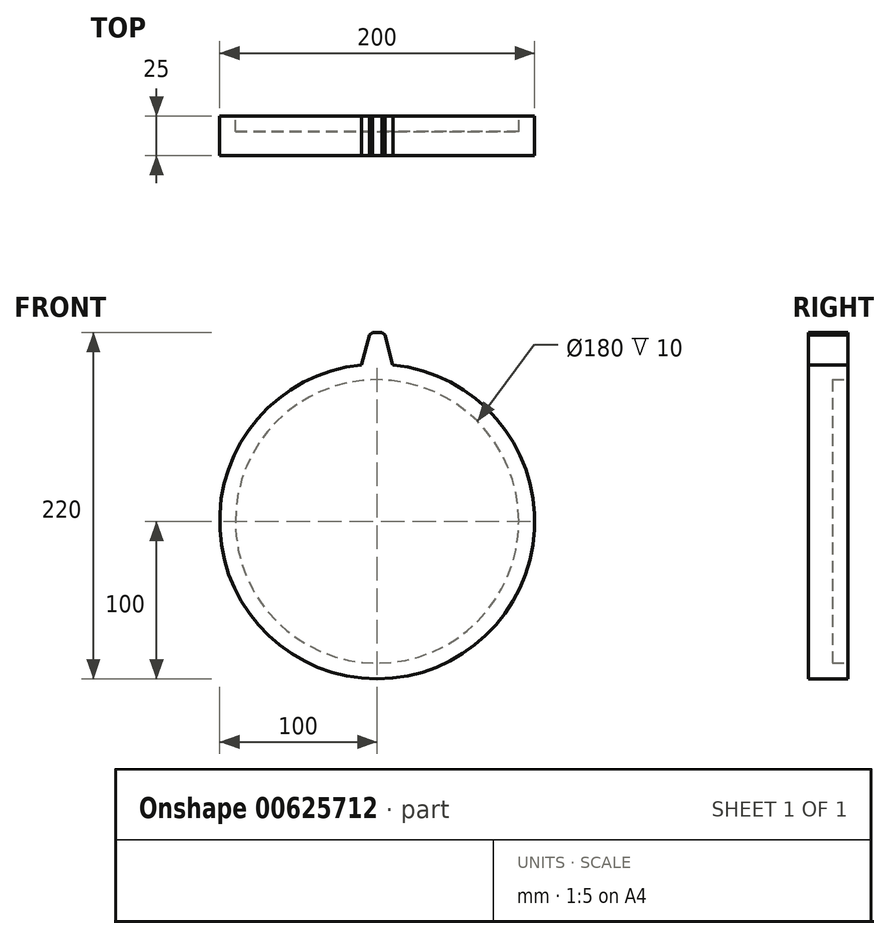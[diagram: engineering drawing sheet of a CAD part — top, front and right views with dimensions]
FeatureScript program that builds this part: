
annotation { "Feature Type Name" : "Feature", "Feature Type Description" : "" }
export const myFeature = defineFeature(function(context is Context, id is Id, definition is map)
    precondition{}
    {
        {
            var Q0;
            Q0=qCreatedBy(makeId("Front.planeOp"),FACE);
            var sketch = newSketch(context, id + "F0", { "sketchPlane" : qUnion([Q0])});
            skCircle(sketch, "E0", {"center": v(0, 0) * mm, "radius": 100 * mm});
            skSolve(sketch);
        }
        {
            var Q0;
            Q0=makeQuery(id+"F0.imprint","IMPRINT",FACE,{"disambiguationData":[TD([[makeQuery(id+"F0.imprint","IMPRINT",EDGE,{"derivedFrom":sQuery(id+"F0.wireOp",EDGE,"E0")}),1.0]])]});
            extrude(context, id + "F1", {"entities" : qUnion([Q0]), "depth" : 25 * mm, "offsetDistance" : 25 * mm});
        }
        {
            var Q0;
            Q0=qCreatedBy(makeId("Front.planeOp"),FACE);
            var sketch = newSketch(context, id + "F2", { "sketchPlane" : qUnion([Q0])});
            skLineSegment(sketch, "E1", {"start": v(-10, 99.5) * mm, "end": v(-4.5, 120) * mm});
            skLineSegment(sketch, "E2", {"start": v(-4.5, 120) * mm, "end": v(4.5, 120) * mm});
            skLineSegment(sketch, "E3", {"start": v(4.5, 120) * mm, "end": v(10, 99.5) * mm});
            skLineSegment(sketch, "E4", {"start": v(10, 99.5) * mm, "end": v(-10, 99.5) * mm});
            skSolve(sketch);
        }
        {
            var Q0;
            Q0 = qSketchRegion(id + "F2", true);
            extrude(context, id + "F3", {"entities" : qUnion([Q0]), "operationType" : NewBodyOperationType.ADD, "depth" : 25 * mm, "offsetDistance" : 25 * mm});
        }
        {
            var Q0;
            Q0=makeQuery(id+"F3.opExtrude","SWEPT_EDGE",EDGE,{"disambiguationData":[OSD([sQuery(id+"F2.wireOp",EDGE,"E1"),sQuery(id+"F2.wireOp",EDGE,"E2")])]});
            var Q1;
            Q1=makeQuery(id+"F3.opExtrude","SWEPT_EDGE",EDGE,{"disambiguationData":[OSD([sQuery(id+"F2.wireOp",EDGE,"E2"),sQuery(id+"F2.wireOp",EDGE,"E3")])]});
            chamfer(context, id + "F4", {"entities" : qUnion([Q0, Q1]), "width" : 2 * mm, "tangentPropagation" : true});
        }
        {
            var Q0;
            Q0=makeQuery(id+"F3.opExtrude","SWEPT_EDGE",EDGE,{"disambiguationData":[OSD([sQuery(id+"F2.wireOp",EDGE,"E1"),sQuery(id+"F2.wireOp",EDGE,"E4")])]});
            var Q1;
            Q1=makeQuery(id+"F3.opExtrude","SWEPT_EDGE",EDGE,{"disambiguationData":[OSD([sQuery(id+"F2.wireOp",EDGE,"E3"),sQuery(id+"F2.wireOp",EDGE,"E4")])]});
            fillet(context, id + "F5", {"entities" : qUnion([Q0, Q1]), "radius" : 5 * mm, "tangentPropagation" : true, "allowEdgeOverflow" : false});
        }
        {
            var Q0;
            {var subQ0=sQuery(id+"F2.wireOp",EDGE,"E4");var subQ1=sQuery(id+"F2.wireOp",EDGE,"E3");var subQ2=sQuery(id+"F2.wireOp",EDGE,"E2");var subQ3=sQuery(id+"F2.wireOp",EDGE,"E1");Q0=makeQuery(id+"FxM7K1GwsqZvOpN_1.19.F3.boolean.opBoolean","MERGE",FACE,{"derivedFrom":[makeQuery(id+"FxM7K1GwsqZvOpN_1.18.F3.boolean.opBoolean","MERGE",FACE,{"derivedFrom":[makeQuery(id+"FxM7K1GwsqZvOpN_1.17.F3.boolean.opBoolean","MERGE",FACE,{"derivedFrom":[makeQuery(id+"FxM7K1GwsqZvOpN_1.16.F3.boolean.opBoolean","MERGE",FACE,{"derivedFrom":[makeQuery(id+"FxM7K1GwsqZvOpN_1.15.F3.boolean.opBoolean","MERGE",FACE,{"derivedFrom":[makeQuery(id+"FxM7K1GwsqZvOpN_1.14.F3.boolean.opBoolean","MERGE",FACE,{"derivedFrom":[makeQuery(id+"FxM7K1GwsqZvOpN_1.13.F3.boolean.opBoolean","MERGE",FACE,{"derivedFrom":[makeQuery(id+"FxM7K1GwsqZvOpN_1.12.F3.boolean.opBoolean","MERGE",FACE,{"derivedFrom":[makeQuery(id+"FxM7K1GwsqZvOpN_1.11.F3.boolean.opBoolean","MERGE",FACE,{"derivedFrom":[makeQuery(id+"FxM7K1GwsqZvOpN_1.10.F3.boolean.opBoolean","MERGE",FACE,{"derivedFrom":[makeQuery(id+"FxM7K1GwsqZvOpN_1.9.F3.boolean.opBoolean","MERGE",FACE,{"derivedFrom":[makeQuery(id+"FxM7K1GwsqZvOpN_1.8.F3.boolean.opBoolean","MERGE",FACE,{"derivedFrom":[makeQuery(id+"FxM7K1GwsqZvOpN_1.7.F3.boolean.opBoolean","MERGE",FACE,{"derivedFrom":[makeQuery(id+"FxM7K1GwsqZvOpN_1.6.F3.boolean.opBoolean","MERGE",FACE,{"derivedFrom":[makeQuery(id+"FxM7K1GwsqZvOpN_1.5.F3.boolean.opBoolean","MERGE",FACE,{"derivedFrom":[makeQuery(id+"FxM7K1GwsqZvOpN_1.4.F3.boolean.opBoolean","MERGE",FACE,{"derivedFrom":[makeQuery(id+"FxM7K1GwsqZvOpN_1.3.F3.boolean.opBoolean","MERGE",FACE,{"derivedFrom":[makeQuery(id+"FxM7K1GwsqZvOpN_1.2.F3.boolean.opBoolean","MERGE",FACE,{"derivedFrom":[makeQuery(id+"FxM7K1GwsqZvOpN_1.1.F3.boolean.opBoolean","MERGE",FACE,{"derivedFrom":[makeQuery(id+"F3.boolean.opBoolean","MERGE",FACE,{"derivedFrom":[makeQuery(id+"F1.opExtrude","CAP_FACE",FACE,{"disambiguationData":[OSD([sQuery(id+"F0.wireOp",EDGE,"E0")])],"isStart":true}),makeQuery(id+"F3.opExtrude","CAP_FACE",FACE,{"disambiguationData":[OSD([subQ3,subQ2,subQ1,subQ0])],"isStart":true})]}),makeQuery(id+"FxM7K1GwsqZvOpN_1.1.F3.opExtrude","CAP_FACE",FACE,{"disambiguationData":[OSD([subQ3,subQ2,subQ1,subQ0])],"isStart":true})]}),makeQuery(id+"FxM7K1GwsqZvOpN_1.2.F3.opExtrude","CAP_FACE",FACE,{"disambiguationData":[OSD([subQ3,subQ2,subQ1,subQ0])],"isStart":true})]}),makeQuery(id+"FxM7K1GwsqZvOpN_1.3.F3.opExtrude","CAP_FACE",FACE,{"disambiguationData":[OSD([subQ3,subQ2,subQ1,subQ0])],"isStart":true})]}),makeQuery(id+"FxM7K1GwsqZvOpN_1.4.F3.opExtrude","CAP_FACE",FACE,{"disambiguationData":[OSD([subQ3,subQ2,subQ1,subQ0])],"isStart":true})]}),makeQuery(id+"FxM7K1GwsqZvOpN_1.5.F3.opExtrude","CAP_FACE",FACE,{"disambiguationData":[OSD([subQ3,subQ2,subQ1,subQ0])],"isStart":true})]}),makeQuery(id+"FxM7K1GwsqZvOpN_1.6.F3.opExtrude","CAP_FACE",FACE,{"disambiguationData":[OSD([subQ3,subQ2,subQ1,subQ0])],"isStart":true})]}),makeQuery(id+"FxM7K1GwsqZvOpN_1.7.F3.opExtrude","CAP_FACE",FACE,{"disambiguationData":[OSD([subQ3,subQ2,subQ1,subQ0])],"isStart":true})]}),makeQuery(id+"FxM7K1GwsqZvOpN_1.8.F3.opExtrude","CAP_FACE",FACE,{"disambiguationData":[OSD([subQ3,subQ2,subQ1,subQ0])],"isStart":true})]}),makeQuery(id+"FxM7K1GwsqZvOpN_1.9.F3.opExtrude","CAP_FACE",FACE,{"disambiguationData":[OSD([subQ3,subQ2,subQ1,subQ0])],"isStart":true})]}),makeQuery(id+"FxM7K1GwsqZvOpN_1.10.F3.opExtrude","CAP_FACE",FACE,{"disambiguationData":[OSD([subQ3,subQ2,subQ1,subQ0])],"isStart":true})]}),makeQuery(id+"FxM7K1GwsqZvOpN_1.11.F3.opExtrude","CAP_FACE",FACE,{"disambiguationData":[OSD([subQ3,subQ2,subQ1,subQ0])],"isStart":true})]}),makeQuery(id+"FxM7K1GwsqZvOpN_1.12.F3.opExtrude","CAP_FACE",FACE,{"disambiguationData":[OSD([subQ3,subQ2,subQ1,subQ0])],"isStart":true})]}),makeQuery(id+"FxM7K1GwsqZvOpN_1.13.F3.opExtrude","CAP_FACE",FACE,{"disambiguationData":[OSD([subQ3,subQ2,subQ1,subQ0])],"isStart":true})]}),makeQuery(id+"FxM7K1GwsqZvOpN_1.14.F3.opExtrude","CAP_FACE",FACE,{"disambiguationData":[OSD([subQ3,subQ2,subQ1,subQ0])],"isStart":true})]}),makeQuery(id+"FxM7K1GwsqZvOpN_1.15.F3.opExtrude","CAP_FACE",FACE,{"disambiguationData":[OSD([subQ3,subQ2,subQ1,subQ0])],"isStart":true})]}),makeQuery(id+"FxM7K1GwsqZvOpN_1.16.F3.opExtrude","CAP_FACE",FACE,{"disambiguationData":[OSD([subQ3,subQ2,subQ1,subQ0])],"isStart":true})]}),makeQuery(id+"FxM7K1GwsqZvOpN_1.17.F3.opExtrude","CAP_FACE",FACE,{"disambiguationData":[OSD([subQ3,subQ2,subQ1,subQ0])],"isStart":true})]}),makeQuery(id+"FxM7K1GwsqZvOpN_1.18.F3.opExtrude","CAP_FACE",FACE,{"disambiguationData":[OSD([subQ3,subQ2,subQ1,subQ0])],"isStart":true})]}),makeQuery(id+"FxM7K1GwsqZvOpN_1.19.F3.opExtrude","CAP_FACE",FACE,{"disambiguationData":[OSD([subQ3,subQ2,subQ1,subQ0])],"isStart":true})]});}
            var sketch = newSketch(context, id + "F6", { "sketchPlane" : qUnion([Q0])});
            skCircle(sketch, "E5", {"center": v(0, 0) * mm, "radius": 90 * mm});
            skSolve(sketch);
        }
        {
            var Q0;
            Q0=makeQuery(id+"F6.imprint","IMPRINT",FACE,{"disambiguationData":[TD([[makeQuery(id+"F6.imprint","IMPRINT",EDGE,{"derivedFrom":sQuery(id+"F6.wireOp",EDGE,"E5")}),1.0]])]});
            extrude(context, id + "F7", {"entities" : qUnion([Q0]), "operationType" : NewBodyOperationType.REMOVE, "oppositeDirection" : true, "depth" : 10 * mm, "offsetDistance" : 25 * mm});
        }
    });
